# Revit family: Faucet-Lavatory-KOHLER-Parallel-K-23472ME
name_source: partatom
category: Plumbing Fixtures
units: mm (PartAtom-declared; Revit-internal decimal feet)

## family parameters
Cut with Voids When Loaded = No
Host = Face
OmniClass Number = 23.31.11.00
OmniClass Title = Faucets
Part Type = Normal
Room Calculation Point = No
Round Connector Dimension = Use Diameter
Shared = No

## types (5) — shared parameters
ADA Compliant = No
Assembly Code = D2010
CW Connection = Yes
Cold Water Inlet = Cold Water Inlet
Date Modified = 12/9/2022
Default Elevation = 36"
Description = Single-Handle Bathroom Sink Faucet
Flow Rate = 1 GPM
HW Connection = Yes
Handle Clearance = 3 13/16"
Height = 6 1/8"
Hot Water Inlet = Hot Water Inlet
Length = 4 1/2"
Manufacturer = Kohler Co.
Master Format 2014 = 22 41 39
Master Format 2014 Name = Residential Faucets, Supplies, and Trim
Material = Premium Metal Construction
Pressure = 40.00 psi
Product Documentation Link = https://me.kohler.com
Product Name = Parallel
Spout Reach = 4 1/2"
URL = https://me.kohler.com
Vent Connection = No
Waste Connection = No
Waste Water Outlet = Waste Water Outlet
WaterSense Certified = No
Width = 1 7/8"

## per-type parameters (varying)
| type | 4, With Drain | 4ND, Without Drain | Drain Included | Finish | Model | Product Page URL | Type |
| With Drain, CP-Polished Chrome | Yes | No | Yes | Kohler-Metal-CP-Polished_Chrome | K-23472ME-4-CP | https://me.kohler.com | 1 |
| Without Drain, AF-Vibrant French Gold | No | Yes | No | Kohler-Metal-AF-Vibrant_French_Gold | K-23472ME-4ND-AF |  | 2 |
| Without Drain, BN-Vibrant Brushed Nickel | No | Yes | No | Kohler-Metal-BN-Vibrant_Brushed_Nickel | K-23472ME-4ND-BN |  | 3 |
| Without Drain, BV-Brushed Bronze | No | Yes | No | Kohler-Metal-BV-Brushed_Bronze | K-23472ME-4ND-BV |  | 4 |
| Without Drain, RGD-Polished Rose Gold | No | Yes | No | Kohler-Metal-RGD-Polished_Rose_Gold | K-23472ME-4ND-RGD |  | 5 |

## geometry (parser evidence)
native form markers: Sweep x5
no freeform markers — native parametric forms only
